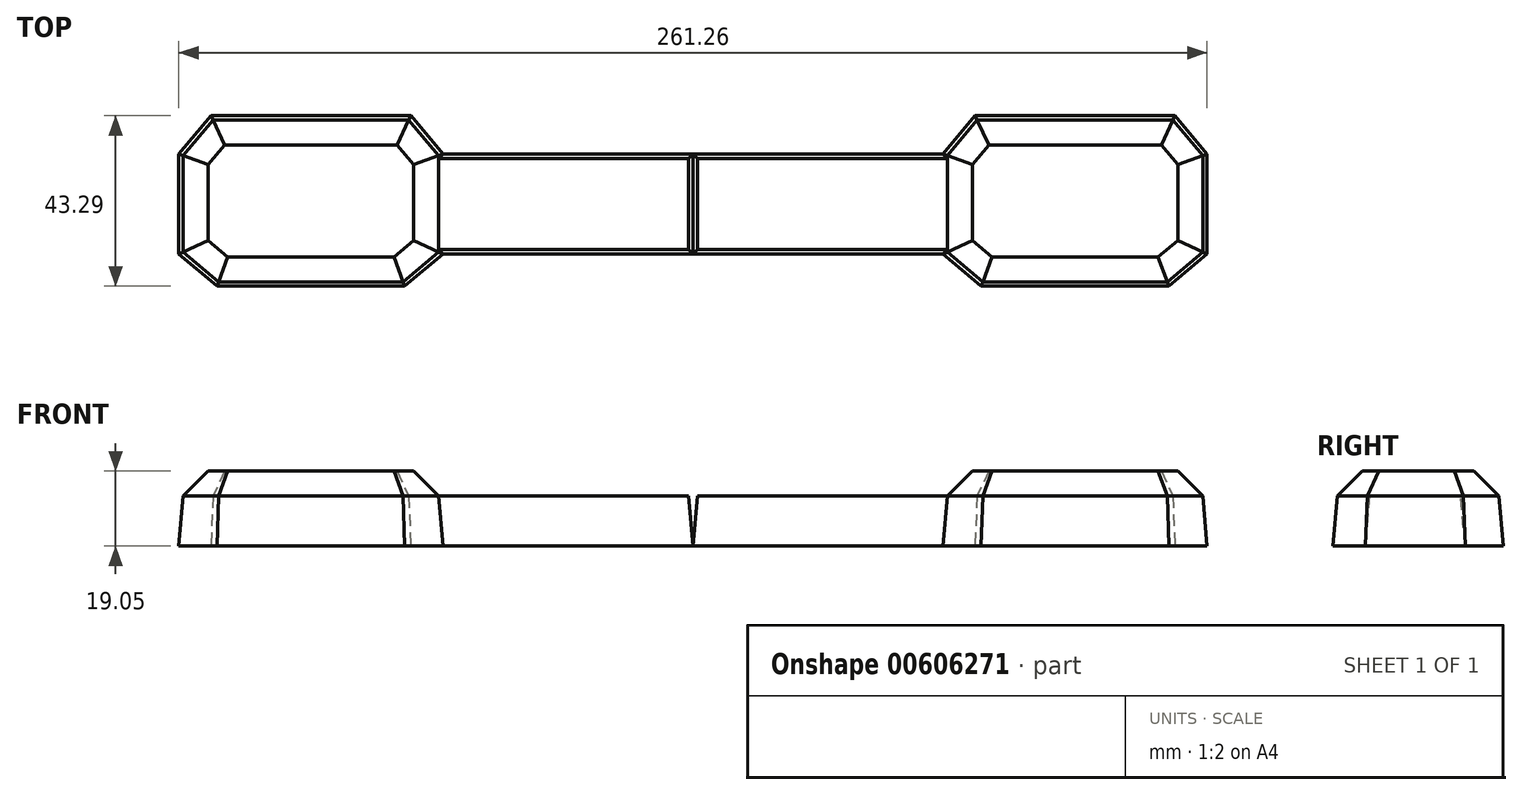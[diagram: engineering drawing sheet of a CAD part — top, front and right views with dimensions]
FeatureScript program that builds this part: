
annotation { "Feature Type Name" : "Feature", "Feature Type Description" : "" }
export const myFeature = defineFeature(function(context is Context, id is Id, definition is map)
    precondition{}
    {
        {
            var Q0;
            Q0=qCreatedBy(makeId("Top.planeOp"),FACE);
            var sketch = newSketch(context, id + "F0", { "sketchPlane" : qUnion([Q0])});
            skLineSegment(sketch, "E0.bottom", {"start": v(63.5, 12.7) * mm, "end": v(-63.5, 12.7) * mm, "construction": true});
            skLineSegment(sketch, "E0.top", {"start": v(63.5, -12.7) * mm, "end": v(-63.5, -12.7) * mm, "construction": true});
            skLineSegment(sketch, "E0.right", {"start": v(-63.5, 12.7) * mm, "end": v(-63.5, -12.7) * mm, "construction": true});
            skPoint(sketch, "E0.middle", {"position": v(0, 0) * mm});
            skLineSegment(sketch, "E1", {"start": v(0, 12.7) * mm, "end": v(0, -12.7) * mm, "construction": true});
            skLineSegment(sketch, "E2.bottom", {"start": v(0, 12.7) * mm, "end": v(63.5, 12.7) * mm});
            skLineSegment(sketch, "E2.top", {"start": v(0, -12.7) * mm, "end": v(63.5, -12.7) * mm});
            skLineSegment(sketch, "E2.left", {"start": v(0, 12.7) * mm, "end": v(0, -12.7) * mm});
            skLineSegment(sketch, "E3", {"start": v(63.5, 12.7) * mm, "end": v(71.66, 22.43) * mm});
            skLineSegment(sketch, "E4", {"start": v(71.66, 22.43) * mm, "end": v(122.46, 22.43) * mm});
            skLineSegment(sketch, "E5", {"start": v(122.46, 22.43) * mm, "end": v(130.63, 12.7) * mm});
            skLineSegment(sketch, "E6", {"start": v(130.63, 12.7) * mm, "end": v(130.63, -12.7) * mm});
            skLineSegment(sketch, "E7", {"start": v(130.63, -12.7) * mm, "end": v(120.9, -20.86) * mm});
            skLineSegment(sketch, "E8", {"start": v(63.5, -12.7) * mm, "end": v(73.23, -20.86) * mm});
            skLineSegment(sketch, "E9", {"start": v(73.23, -20.86) * mm, "end": v(120.9, -20.86) * mm});
            skLineSegment(sketch, "E10", {"start": v(63.5, -12.7) * mm, "end": v(63.5, 12.7) * mm});
            skLineSegment(sketch, "E11", {"start": v(63.5, 12.7) * mm, "end": v(71.24, 12.7) * mm});
            skLineSegment(sketch, "E12", {"start": v(63.5, -12.7) * mm, "end": v(71.24, -12.7) * mm});
            skLineSegment(sketch, "E13", {"start": v(71.24, 12.7) * mm, "end": v(71.24, -12.7) * mm});
            skSolve(sketch);
        }
        {
            var Q0;
            Q0=makeQuery(id+"F0.imprint","IMPRINT",FACE,{"disambiguationData":[TD([[makeQuery(id+"F0.imprint","IMPRINT",EDGE,{"derivedFrom":sQuery(id+"F0.wireOp",EDGE,"E2.bottom")}),-1.0]])]});
            var Q1;
            {var subQ4=sQuery(id+"F0.wireOp",EDGE,"E10");Q1=makeQuery(id+"F0.imprint","IMPRINT",FACE,{"disambiguationData":[TD([[makeQuery(id+"F0.imprint","IMPRINT",EDGE,{"derivedFrom":subQ4}),-1.0]])]});}
            extrude(context, id + "F1", {"entities" : qUnion([Q0, Q1]), "depth" : 12.7 * mm, "offsetDistance" : 25.4 * mm, "hasDraft" : true, "draftAngle" : 5 * degree, "draftPullDirection" : true});
        }
        {
            var Q0;
            {var subQ0=sQuery(id+"F0.wireOp",EDGE,"E4");Q0=makeQuery(id+"F0.imprint","IMPRINT",FACE,{"disambiguationData":[TD([[makeQuery(id+"F0.imprint","IMPRINT",EDGE,{"derivedFrom":subQ0}),-1.0]])]});}
            var Q1;
            {var subQ4=sQuery(id+"F0.wireOp",EDGE,"E10");Q1=makeQuery(id+"F0.imprint","IMPRINT",FACE,{"disambiguationData":[TD([[makeQuery(id+"F0.imprint","IMPRINT",EDGE,{"derivedFrom":subQ4}),-1.0]])]});}
            extrude(context, id + "F2", {"entities" : qUnion([Q0, Q1]), "operationType" : NewBodyOperationType.ADD, "depth" : 12.7 * mm, "offsetDistance" : 25.4 * mm, "hasDraft" : true, "draftAngle" : 5 * degree, "draftPullDirection" : true});
        }
        {
            var Q0;
            Q0=makeQuery(id+"F2.boolean.opBoolean","MERGE",FACE,{"derivedFrom":[makeQuery(id+"F1.opExtrude","CAP_FACE",FACE,{"disambiguationData":[OSD([sQuery(id+"F0.wireOp",EDGE,"E2.bottom"),sQuery(id+"F0.wireOp",EDGE,"E2.top"),sQuery(id+"F0.wireOp",EDGE,"E2.left"),sQuery(id+"F0.wireOp",EDGE,"E11"),sQuery(id+"F0.wireOp",EDGE,"E12"),sQuery(id+"F0.wireOp",EDGE,"E13")])],"isStart":false}),makeQuery(id+"F2.opExtrude","CAP_FACE",FACE,{"disambiguationData":[OSD([sQuery(id+"F0.wireOp",EDGE,"E3"),sQuery(id+"F0.wireOp",EDGE,"E4"),sQuery(id+"F0.wireOp",EDGE,"E5"),sQuery(id+"F0.wireOp",EDGE,"E6"),sQuery(id+"F0.wireOp",EDGE,"E7"),sQuery(id+"F0.wireOp",EDGE,"E8"),sQuery(id+"F0.wireOp",EDGE,"E9"),sQuery(id+"F0.wireOp",EDGE,"E10")])],"isStart":false})]});
            var sketch = newSketch(context, id + "F3", { "sketchPlane" : qUnion([Q0])});
            skLineSegment(sketch, "E14", {"start": v(64.61, 11.59) * mm, "end": v(64.61, -11.59) * mm});
            skSolve(sketch);
        }
        {
            var Q0;
            Q0=makeQuery(id+"F3.imprint","IMPRINT",FACE,{"disambiguationData":[TD([[makeQuery(id+"F3.imprint","IMPRINT",EDGE,{"derivedFrom":sQuery(id+"F3.wireOp",EDGE,"E14")}),1.0]])]});
            extrude(context, id + "F4", {"entities" : qUnion([Q0]), "operationType" : NewBodyOperationType.ADD, "depth" : 6.35 * mm, "offsetDistance" : 25.4 * mm, "hasDraft" : true, "draftAngle" : 45 * degree, "draftPullDirection" : true});
        }
        {
            var Q0;
            Q0=makeQuery(id+"F1.opExtrude","SWEPT_BODY",BODY,{"disambiguationData":[OSD([sQuery(id+"F0.wireOp",EDGE,"E2.bottom"),sQuery(id+"F0.wireOp",EDGE,"E2.top"),sQuery(id+"F0.wireOp",EDGE,"E2.left"),sQuery(id+"F0.wireOp",EDGE,"E11"),sQuery(id+"F0.wireOp",EDGE,"E12"),sQuery(id+"F0.wireOp",EDGE,"E13")])]});
            var Q1;
            Q1=qCreatedBy(makeId("Right.planeOp"),FACE);
            mirror(context, id + "F5", {"entities" : qUnion([Q0]), "mirrorPlane" : qUnion([Q1])});
        }
    });
